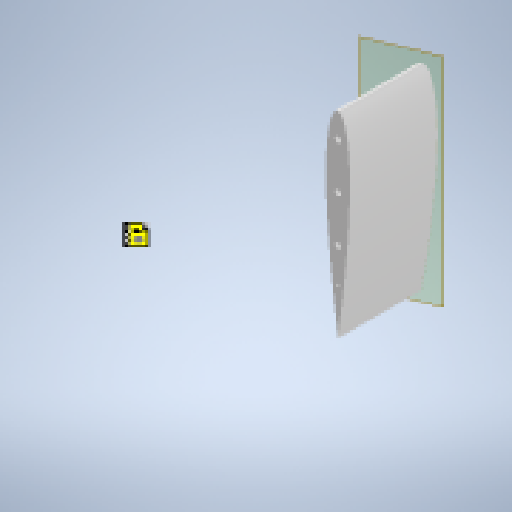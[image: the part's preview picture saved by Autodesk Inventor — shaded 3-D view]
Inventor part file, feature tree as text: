
AUTODESK INVENTOR PART (.ipt)
format: ipt  version: 2025.2 (Build 292293000, 293)  size: 247,296 bytes
history: native  units: in
note: dims shown in document units (in); Inventor stores cm internally (conversion verified against a paired STEP export)
features: extrude x5, sketch x5, plane x4, other x2
ambient origin geometry x8: Origin, YZ Plane, XZ Plane, XY Plane, X Axis, Y Axis, Z Axis, Center Point
bodies: Body1 (feature_tree)
feature tree (16):
  plane  "Work Plane1"
  plane  "Work Plane5"
  extrude  "Extrusion11"  Depth=20.0in TaperAngle=0.0deg
  extrude  "Extrusion14"  Depth=0.125in
  extrude  "Extrusion15"  Depth=0.3937in TaperAngle=0.0deg
  other  "Work Point5"
  extrude  "Extrusion16"  Depth=0.5in
  other  "Work Point6"
  plane  "Work Plane9"
  plane  "Work Plane10"
  extrude  "Extrusion17"  Depth=0.5in
  sketch  "Sketch15"  dims[d38=3.6196in d39=0.0in d55=20.0in d56=0.0in]
  sketch  "Sketch21"  dims[d57=22.5deg d58=0.125in]
  sketch  "Sketch22"  dims[d60=0.3937in d61=0.0in d71=1.0in d72=0.0in]
  sketch  "Sketch23"  dims[d90=0.5in d91=0.0in]
  sketch  "Sketch28"  dims[d92=0.25in d93=0.25in d94=0.25in d96=1.8675in d97=1.8671in d98=0.25in d99=0.25in d100=0.25in d101=1.8675in d102=1.8671in d6=0.5in d7=0.0344in d8=0.5in d9=0.0344in d43=0.5in d44=0.0344in d45=0.5in d46=0.0344in]
